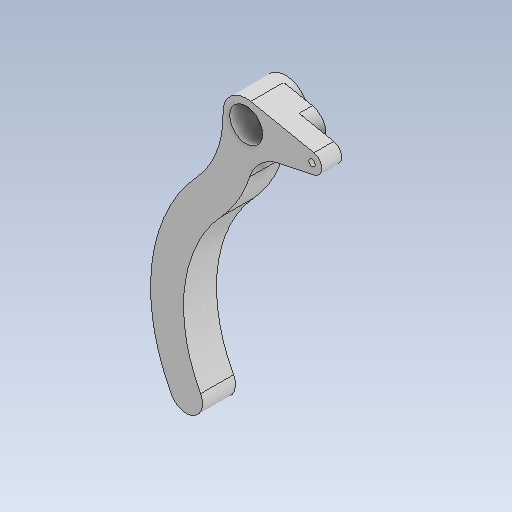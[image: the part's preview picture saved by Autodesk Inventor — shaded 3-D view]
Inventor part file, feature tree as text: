
AUTODESK INVENTOR PART (.ipt)
format: ipt  version: 2020 (Build 240168000, 168)  size: 130,560 bytes
history: native  units: in
note: dims shown in document units (in); Inventor stores cm internally (conversion verified against a paired STEP export)
features: other x3, sketch x3
ambient origin geometry x8: Origin, YZ Plane, XZ Plane, XY Plane, X Axis, Y Axis, Z Axis, Center Point
bodies: Solid1 (feature_tree)
feature tree (6):
  other  "claw-w.ipt"
  other  "Solid1::claw-w.ipt"
  other  "TaggingFeature1"
  sketch  "Sketch1"  dims[d0=0.3937in]
  sketch  "Sketch2"
  sketch  "Sketch3"
